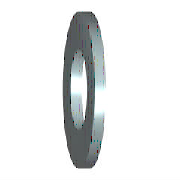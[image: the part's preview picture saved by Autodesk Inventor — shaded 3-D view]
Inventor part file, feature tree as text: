
AUTODESK INVENTOR PART (.ipt)
format: ipt  version: 2020 (Build 240168000, 168)  size: 110,592 bytes
history: native  units: mm (DEFAULTED — no unit token found)
features: other x1, plane x1, sketch x1
ambient origin geometry x7: Origin, YZ Plane, XY Plane, X Axis, Y Axis, Z Axis, Center Point
bodies: Solid1 (feature_tree), Body (feature_tree)
feature tree (3):
  other  "Work Axis1"
  plane  "Work Plane1"
  sketch  "Sketch"  dims[d0=8.4mm d1=16.0mm d2=1.6mm d3=0.0mm d4=0.0mm d5=0.0mm d6=0.0mm d7=0.0mm]
